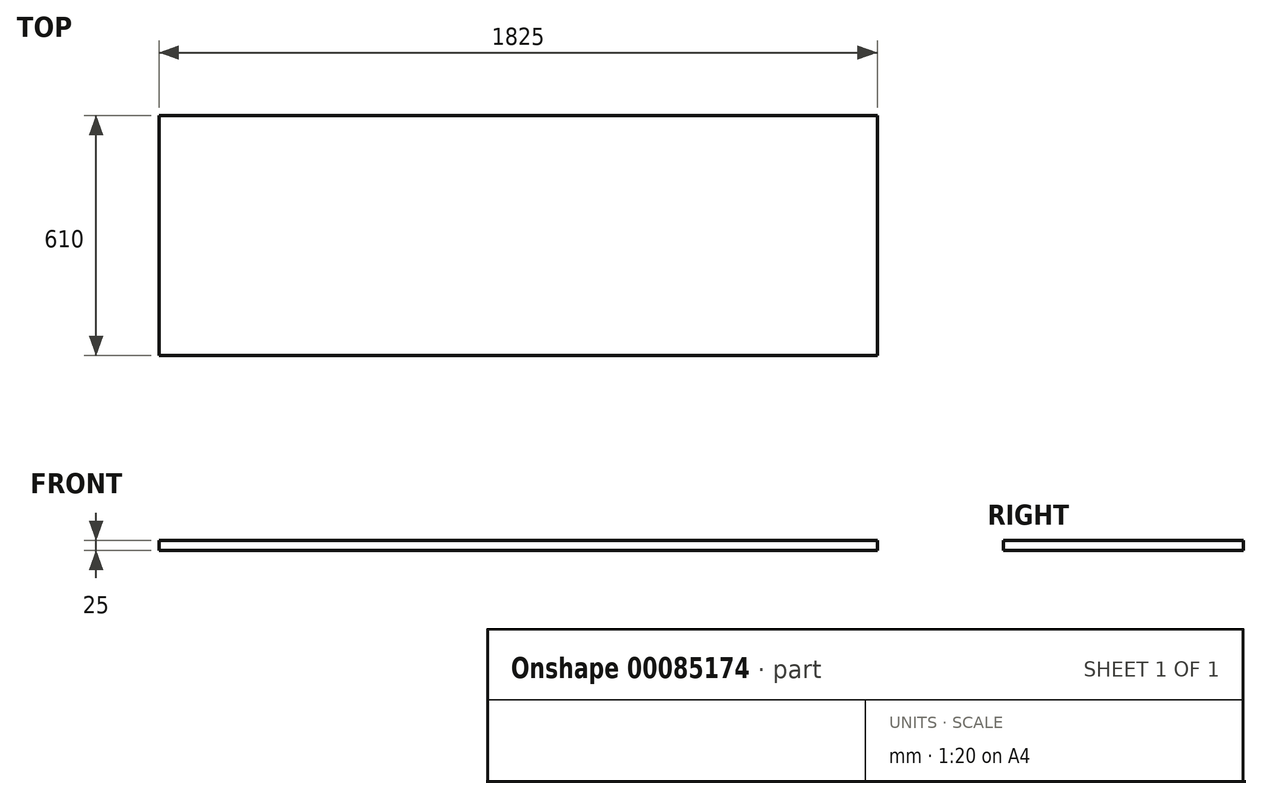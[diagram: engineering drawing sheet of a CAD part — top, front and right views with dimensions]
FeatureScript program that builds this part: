
annotation { "Feature Type Name" : "Feature", "Feature Type Description" : "" }
export const myFeature = defineFeature(function(context is Context, id is Id, definition is map)
    precondition{}
    {
        {
            var Q0;
            Q0=qCreatedBy(makeId("Top.planeOp"),FACE);
            var sketch = newSketch(context, id + "F0", { "sketchPlane" : qUnion([Q0])});
            skLineSegment(sketch, "E0.bottom", {"start": v(912.5, -305) * mm, "end": v(-912.5, -305) * mm});
            skLineSegment(sketch, "E0.top", {"start": v(912.5, 305) * mm, "end": v(-912.5, 305) * mm});
            skLineSegment(sketch, "E0.left", {"start": v(912.5, -305) * mm, "end": v(912.5, 305) * mm});
            skLineSegment(sketch, "E0.right", {"start": v(-912.5, -305) * mm, "end": v(-912.5, 305) * mm});
            skPoint(sketch, "E0.middle", {"position": v(0, 0) * mm});
            skSolve(sketch);
        }
        {
            var Q0;
            Q0 = qSketchRegion(id + "F0", true);
            extrude(context, id + "F1", {"entities" : qUnion([Q0]), "depth" : 25 * mm});
        }
    });
